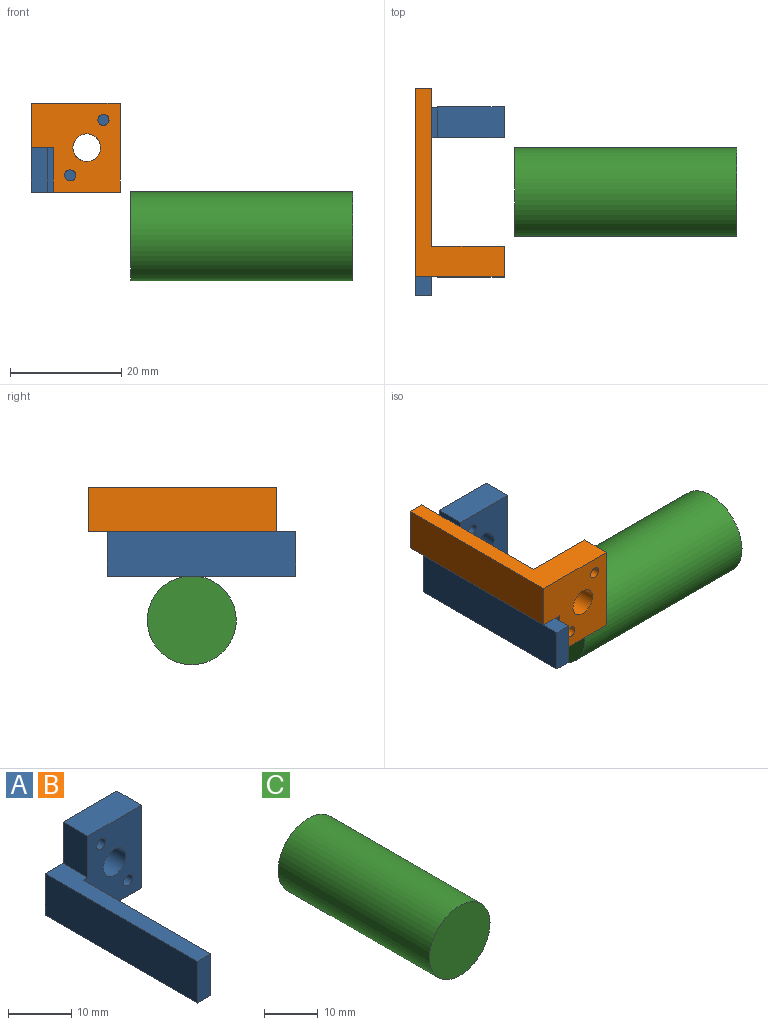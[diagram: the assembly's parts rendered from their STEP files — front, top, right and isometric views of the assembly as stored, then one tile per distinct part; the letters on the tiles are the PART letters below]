
ASSEMBLY  parts=3 mates=2
PART A: 13 faces, bbox 16x34x16 mm
  f0: plane 12x5.5mm, normal (0,0,1), area 66mm2, adj f3,f4,f5,f7
  f1: plane 34x8mm, normal (-1,0,0), area 272mm2, adj f2,f5,f6,f12
  f2: plane 34x16mm, normal (0,0,-1), area 173.5mm2, adj f1,f3,f4,f5,f11,f12
  f3: plane 16x5.5mm, normal (1,0,0), area 88mm2, adj f0,f2,f4,f5
  f4: plane 16x13mm, normal (0,-1,0), area 174.1mm2, adj f0,f2,f3,f6,f7,f8,f9,f10
  f5: plane 16x16mm, normal (0,1,0), area 198.1mm2, adj f0,f1,f2,f3,f6,f7,f8,f9
  f6: plane 34x4mm, normal (0,0,1), area 107.5mm2, adj f1,f4,f5,f7,f11,f12
  f7: plane 8x5.5mm, normal (-1,0,0), area 44mm2, adj f0,f4,f5,f6
  f8: cylinder r=1mm len=5.5mm, axis (0,-1,0), area 34.6mm2, adj f4,f5
  f9: cylinder r=2.5mm len=5.5mm, axis (0,-1,0), area 86.4mm2, adj f4,f5
  f10: cylinder r=1mm len=5.5mm, axis (0,-1,0), area 34.6mm2, adj f4,f5
  f11: plane 28.5x8mm, normal (1,0,0), area 228mm2, adj f2,f4,f6,f12
  f12: plane 8x3mm, normal (0,-1,0), area 24mm2, adj f1,f2,f6,f11
PART B: same geometry as A
PART C: 3 faces, bbox 16x40x16 mm
  f0: cylinder r=8mm len=40mm, axis (0,1,0), area 2010.6mm2, adj f1,f2
  f1: plane 16x16mm, normal (0,-1,0), area 201.1mm2, adj f0
  f2: plane 16x16mm, normal (0,1,0), area 201.1mm2, adj f0
PLACE A t=(13.02,-19.53,9.94)mm fixed
PLACE B rot(axis=(1,0,0),180deg) t=(13.02,-50.13,-6.06)mm
PLACE C rot(axis=(0.67,0.67,-0.33),143.1deg) t=(54.9,-34.79,-14.02)mm
MATE parallel C.f0 <-> B.f11  axis (-1,0,0) through (14.9,-34.79,-14.02)mm
MATE slider A.f4 <-> B.f4  axis (0,-1,0) through (0.02,-25.03,1.94)mm
